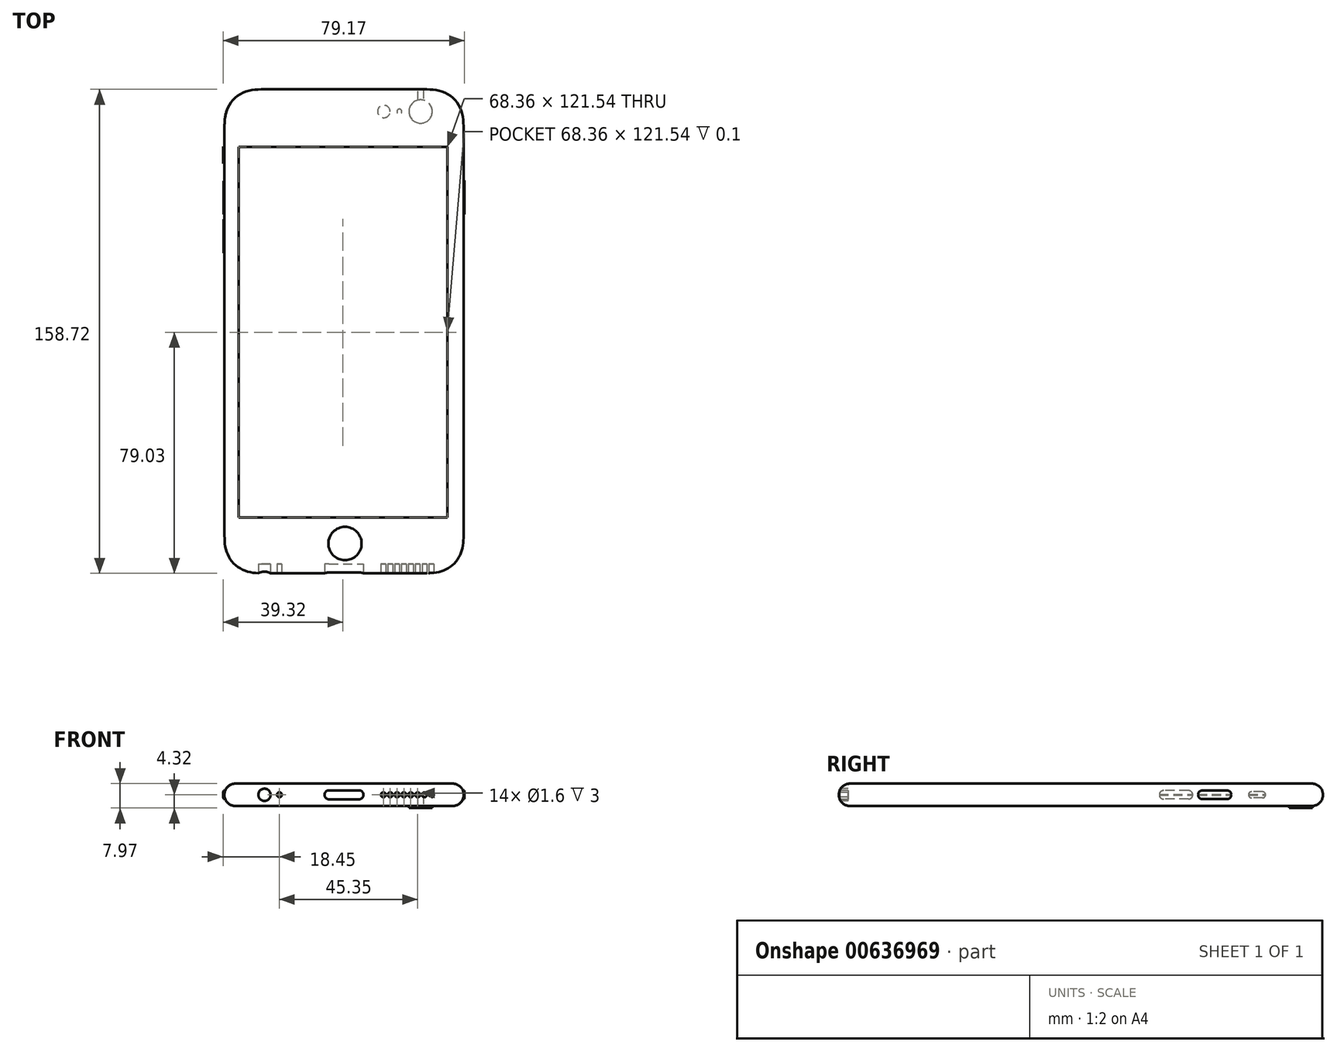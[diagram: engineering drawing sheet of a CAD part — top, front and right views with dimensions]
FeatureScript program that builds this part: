
annotation { "Feature Type Name" : "Feature", "Feature Type Description" : "" }
export const myFeature = defineFeature(function(context is Context, id is Id, definition is map)
    precondition{}
    {
        {
            var Q0;
            Q0=qCreatedBy(makeId("Top.planeOp"),FACE);
            var sketch = newSketch(context, id + "F0", { "sketchPlane" : qUnion([Q0])});
            skLineSegment(sketch, "E0.rect.bottom", {"start": v(25.09, -79.36) * mm, "end": v(-25.09, -79.36) * mm});
            skLineSegment(sketch, "E0.rect.top", {"start": v(25.09, 79.36) * mm, "end": v(-25.09, 79.36) * mm});
            skLineSegment(sketch, "E0.rect.left", {"start": v(39.22, -65.23) * mm, "end": v(39.22, 65.23) * mm});
            skLineSegment(sketch, "E0.rect.right", {"start": v(-39.22, -65.23) * mm, "end": v(-39.22, 65.23) * mm});
            skPoint(sketch, "E0.rect.middle", {"position": v(0, 0) * mm});
            skCircle(sketch, "E1", {"center": v(25.12, 72.09) * mm, "radius": 3.83 * mm});
            skCircle(sketch, "E2", {"center": v(18.16, 72.09) * mm, "radius": 0.8 * mm});
            skCircle(sketch, "E3", {"center": v(13.06, 72.09) * mm, "radius": 2.06 * mm});
            skLineSegment(sketch, "E4", {"start": v(-39.22, 72.1) * mm, "end": v(39.22, 72.1) * mm, "construction": true});
            skPoint(sketch, "E5.visualSharp", {"position": v(-39.22, 79.36) * mm});
            skFitSpline(sketch, "E6", {"points": [v(-25.09, 79.36) * mm, v(-29.02, 79.25) * mm, v(-32.83, 78.38) * mm, v(-36.09, 76.23) * mm, v(-38.24, 72.97) * mm, v(-39.1, 69.16) * mm, v(-39.22, 65.23) * mm], "startDerivative": vector(-8.98, 0) * mm, "endDerivative": vector(0, -8.98) * mm});
            skLineSegment(sketch, "E7", {"start": v(-25.09, 79.36) * mm, "end": v(-39.22, 79.36) * mm, "construction": true});
            skLineSegment(sketch, "E8", {"start": v(-39.22, 79.36) * mm, "end": v(-39.22, 65.23) * mm, "construction": true});
            skLineSegment(sketch, "E9", {"start": v(0, 79.36) * mm, "end": v(0, -79.36) * mm, "construction": true});
            skLineSegment(sketch, "E10", {"start": v(-39.22, 0) * mm, "end": v(39.22, 0) * mm, "construction": true});
            skFitSpline(sketch, "E11.MirrorCS", {"points": [v(25.09, 79.36) * mm, v(29.02, 79.25) * mm, v(32.83, 78.38) * mm, v(36.09, 76.23) * mm, v(38.24, 72.97) * mm, v(39.1, 69.16) * mm, v(39.22, 65.23) * mm], "startDerivative": vector(8.98, 0) * mm, "endDerivative": vector(0, -8.98) * mm});
            skFitSpline(sketch, "E12.MirrorCS", {"points": [v(-25.09, -79.36) * mm, v(-29.02, -79.25) * mm, v(-32.83, -78.38) * mm, v(-36.09, -76.23) * mm, v(-38.24, -72.97) * mm, v(-39.1, -69.16) * mm, v(-39.22, -65.23) * mm], "startDerivative": vector(-8.98, 0) * mm, "endDerivative": vector(0, 8.98) * mm});
            skFitSpline(sketch, "E13.MirrorCS", {"points": [v(25.09, -79.36) * mm, v(29.02, -79.25) * mm, v(32.83, -78.38) * mm, v(36.09, -76.23) * mm, v(38.24, -72.97) * mm, v(39.1, -69.16) * mm, v(39.22, -65.23) * mm], "startDerivative": vector(8.98, 0) * mm, "endDerivative": vector(0, 8.98) * mm});
            skCircle(sketch, "E14", {"center": v(0, 37.36) * mm, "radius": 11 * mm, "construction": true});
            skSolve(sketch);
        }
        {
            var Q0;
            Q0=makeQuery(id+"F0.imprint","IMPRINT",FACE,{"disambiguationData":[TD([[makeQuery(id+"F0.imprint","IMPRINT",EDGE,{"derivedFrom":sQuery(id+"F0.wireOp",EDGE,"E0.rect.bottom")}),-1.0]])]});
            var Q1;
            Q1=makeQuery(id+"F0.imprint","IMPRINT",FACE,{"disambiguationData":[TD([[makeQuery(id+"F0.imprint","IMPRINT",EDGE,{"derivedFrom":sQuery(id+"F0.wireOp",EDGE,"E1")}),1.0]])]});
            var Q2;
            Q2=makeQuery(id+"F0.imprint","IMPRINT",FACE,{"disambiguationData":[TD([[makeQuery(id+"F0.imprint","IMPRINT",EDGE,{"derivedFrom":sQuery(id+"F0.wireOp",EDGE,"E2")}),1.0]])]});
            var Q3;
            Q3=makeQuery(id+"F0.imprint","IMPRINT",FACE,{"disambiguationData":[TD([[makeQuery(id+"F0.imprint","IMPRINT",EDGE,{"derivedFrom":sQuery(id+"F0.wireOp",EDGE,"E3")}),1.0]])]});
            extrude(context, id + "F1", {"entities" : qUnion([Q0, Q1, Q2, Q3]), "depth" : 7.3 * mm});
        }
        {
            var Q0;
            Q0=makeQuery(id+"F0.imprint","IMPRINT",FACE,{"disambiguationData":[TD([[makeQuery(id+"F0.imprint","IMPRINT",EDGE,{"derivedFrom":sQuery(id+"F0.wireOp",EDGE,"E1")}),1.0]])]});
            extrude(context, id + "F2", {"entities" : qUnion([Q0]), "operationType" : NewBodyOperationType.ADD, "oppositeDirection" : true, "depth" : 0.67 * mm});
        }
        {
            var Q0;
            Q0=makeQuery(id+"F0.imprint","IMPRINT",FACE,{"disambiguationData":[TD([[makeQuery(id+"F0.imprint","IMPRINT",EDGE,{"derivedFrom":sQuery(id+"F0.wireOp",EDGE,"E3")}),1.0]])]});
            var Q1;
            Q1=makeQuery(id+"F0.imprint","IMPRINT",FACE,{"disambiguationData":[TD([[makeQuery(id+"F0.imprint","IMPRINT",EDGE,{"derivedFrom":sQuery(id+"F0.wireOp",EDGE,"E2")}),1.0]])]});
            extrude(context, id + "F3", {"entities" : qUnion([Q0, Q1]), "operationType" : NewBodyOperationType.REMOVE, "depth" : 0.1 * mm});
        }
        {
            var Q0;
            Q0=makeQuery(id+"F1.opExtrude","CAP_FACE",FACE,{"disambiguationData":[OSD([sQuery(id+"F0.wireOp",EDGE,"E0.rect.bottom"),sQuery(id+"F0.wireOp",EDGE,"E0.rect.top"),sQuery(id+"F0.wireOp",EDGE,"E0.rect.left"),sQuery(id+"F0.wireOp",EDGE,"E0.rect.right"),sQuery(id+"F0.wireOp",EDGE,"d7852d5b-fe0f-4a90-bdf2-04cff158e1f8.filletArc"),sQuery(id+"F0.wireOp",EDGE,"E5.filletArc"),sQuery(id+"F0.wireOp",EDGE,"7c06d2e9-cdf6-4879-9dee-aab3bc7c6033.filletArc"),sQuery(id+"F0.wireOp",EDGE,"93b3bdb9-dbb8-49f8-8f1e-002f612095da.filletArc")])],"isStart":false});
            var sketch = newSketch(context, id + "F4", { "sketchPlane" : qUnion([Q0])});
            skCircle(sketch, "E15", {"center": v(0.32, -69.6) * mm, "radius": 5.45 * mm});
            skLineSegment(sketch, "E16.bottom", {"start": v(-34.51, 60.44) * mm, "end": v(33.85, 60.44) * mm});
            skLineSegment(sketch, "E16.top", {"start": v(-34.5, -61.1) * mm, "end": v(33.85, -61.1) * mm});
            skLineSegment(sketch, "E16.left", {"start": v(-34.51, 60.44) * mm, "end": v(-34.5, -61.1) * mm});
            skLineSegment(sketch, "E16.right", {"start": v(33.85, 60.44) * mm, "end": v(33.85, -61.1) * mm});
            skSolve(sketch);
        }
        {
            var Q0;
            Q0=makeQuery(id+"F4.imprint","IMPRINT",FACE,{"disambiguationData":[TD([[makeQuery(id+"F4.imprint","IMPRINT",EDGE,{"derivedFrom":sQuery(id+"F4.wireOp",EDGE,"E15")}),1.0]])]});
            extrude(context, id + "F5", {"entities" : qUnion([Q0]), "operationType" : NewBodyOperationType.REMOVE, "oppositeDirection" : true, "depth" : 0.1 * mm});
        }
        {
            var Q0;
            Q0=makeQuery(id+"F4.imprint","IMPRINT",FACE,{"disambiguationData":[TD([[makeQuery(id+"F4.imprint","IMPRINT",EDGE,{"derivedFrom":sQuery(id+"F4.wireOp",EDGE,"E16.bottom")}),-1.0]])]});
            extrude(context, id + "F6", {"entities" : qUnion([Q0]), "operationType" : NewBodyOperationType.REMOVE, "oppositeDirection" : true, "depth" : 0.1 * mm});
        }
        {
            var Q0;
            Q0=makeQuery(id+"F1.opExtrude","SWEPT_FACE",FACE,{"disambiguationData":[OSD([sQuery(id+"F0.wireOp",EDGE,"E0.rect.bottom")])]});
            var sketch = newSketch(context, id + "F7", { "sketchPlane" : qUnion([Q0])});
            skLineSegment(sketch, "E17.0", {"start": v(25.09, 7.3) * mm, "end": v(-25.09, 7.3) * mm, "construction": true});
            skLineSegment(sketch, "E17.1", {"start": v(25.09, 0) * mm, "end": v(-25.09, 0) * mm, "construction": true});
            skLineSegment(sketch, "E17.2", {"start": v(39.22, 7.3) * mm, "end": v(39.22, 0) * mm, "construction": true});
            skLineSegment(sketch, "E17.3", {"start": v(-39.22, 7.3) * mm, "end": v(-39.22, 0) * mm, "construction": true});
            skFitSpline(sketch, "E17.4", {"points": [v(-24.74, 7.3) * mm, v(-29.45, 7.3) * mm, v(-34.16, 7.3) * mm, v(-38.87, 7.3) * mm], "construction": true});
            skFitSpline(sketch, "E17.5", {"points": [v(-24.74, 0) * mm, v(-29.45, 0) * mm, v(-34.16, 0) * mm, v(-38.87, 0) * mm], "construction": true});
            skFitSpline(sketch, "E17.6", {"points": [v(24.74, 0) * mm, v(29.45, 0) * mm, v(34.16, 0) * mm, v(38.87, 0) * mm], "construction": true});
            skFitSpline(sketch, "E17.7", {"points": [v(24.74, 7.3) * mm, v(29.45, 7.3) * mm, v(34.16, 7.3) * mm, v(38.87, 7.3) * mm], "construction": true});
            skLineSegment(sketch, "E18", {"start": v(0, 7.3) * mm, "end": v(0, 0) * mm, "construction": true});
            skLineSegment(sketch, "E19", {"start": v(-39.22, 3.65) * mm, "end": v(-6.4, 3.65) * mm, "construction": true});
            skLineSegment(sketch, "E20", {"start": v(-4.92, 5.12) * mm, "end": v(4.92, 5.12) * mm});
            skLineSegment(sketch, "E21", {"start": v(-4.92, 2.17) * mm, "end": v(4.92, 2.17) * mm});
            skLineSegment(sketch, "E22", {"start": v(-6.4, 3.65) * mm, "end": v(39.22, 3.65) * mm, "construction": true});
            skArc(sketch, "E23", {"start": v(-4.92, 5.13) * mm, "mid": v(-6.4, 3.65) * mm, "end": v(-4.92, 2.17) * mm});
            skArc(sketch, "E24", {"start": v(-4.92, 2.17) * mm, "mid": v(-3.44, 3.65) * mm, "end": v(-4.92, 5.13) * mm, "construction": true});
            skArc(sketch, "E25", {"start": v(4.92, 5.13) * mm, "mid": v(5.96, 4.7) * mm, "end": v(6.4, 3.65) * mm});
            skArc(sketch, "E26", {"start": v(4.92, 2.17) * mm, "mid": v(3.44, 3.65) * mm, "end": v(4.92, 5.13) * mm, "construction": true});
            skArc(sketch, "E27", {"start": v(6.4, 3.65) * mm, "mid": v(5.96, 2.6) * mm, "end": v(4.92, 2.17) * mm});
            skCircle(sketch, "E28", {"center": v(-26.09, 3.65) * mm, "radius": 2 * mm});
            skCircle(sketch, "E29", {"center": v(-21.2, 3.65) * mm, "radius": 0.8 * mm});
            skCircle(sketch, "E30", {"center": v(12.9, 3.65) * mm, "radius": 0.8 * mm});
            skCircle(sketch, "E31.1.0.0", {"center": v(15.15, 3.65) * mm, "radius": 0.8 * mm});
            skCircle(sketch, "E31.2.0.0", {"center": v(17.4, 3.65) * mm, "radius": 0.8 * mm});
            skCircle(sketch, "E31.3.0.0", {"center": v(19.65, 3.65) * mm, "radius": 0.8 * mm});
            skCircle(sketch, "E31.4.0.0", {"center": v(21.9, 3.65) * mm, "radius": 0.8 * mm});
            skCircle(sketch, "E31.5.0.0", {"center": v(24.15, 3.65) * mm, "radius": 0.8 * mm});
            skCircle(sketch, "E31.6.0.0", {"center": v(26.4, 3.65) * mm, "radius": 0.8 * mm});
            skCircle(sketch, "E31.7.0.0", {"center": v(28.65, 3.65) * mm, "radius": 0.8 * mm});
            skLineSegment(sketch, "E31.direction1", {"start": v(12.9, 3.65) * mm, "end": v(15.15, 3.65) * mm, "construction": true});
            skPoint(sketch, "E32", {"position": v(12.1, 3.65) * mm});
            skPoint(sketch, "E33", {"position": v(29.45, 3.65) * mm});
            skLineSegment(sketch, "E34.0", {"start": v(-25.09, 7.3) * mm, "end": v(-25.09, 0) * mm, "construction": true});
            skLineSegment(sketch, "E34.1", {"start": v(25.09, 7.3) * mm, "end": v(25.09, 0) * mm, "construction": true});
            skSolve(sketch);
        }
        {
            var Q0;
            Q0=makeQuery(id+"F1.opExtrude","SWEPT_FACE",FACE,{"disambiguationData":[OSD([sQuery(id+"F0.wireOp",EDGE,"E0.rect.left")])]});
            var sketch = newSketch(context, id + "F8", { "sketchPlane" : qUnion([Q0])});
            skLineSegment(sketch, "E35", {"start": v(-65.23, 2.25) * mm, "end": v(65.23, 2.25) * mm, "construction": true});
            skLineSegment(sketch, "E36", {"start": v(8.97, 4.69) * mm, "end": v(22.34, 4.7) * mm});
            skLineSegment(sketch, "E37", {"start": v(8.97, 2.25) * mm, "end": v(22.34, 2.25) * mm});
            skPoint(sketch, "E38", {"position": v(7.75, 3.47) * mm});
            skPoint(sketch, "E39", {"position": v(23.56, 3.47) * mm});
            skLineSegment(sketch, "E40", {"start": v(39.81, 2.25) * mm, "end": v(47.95, 2.25) * mm});
            skLineSegment(sketch, "E41", {"start": v(39.81, 5.05) * mm, "end": v(39.81, 5.05) * mm});
            skLineSegment(sketch, "E42", {"start": v(39.81, 3.65) * mm, "end": v(47.95, 3.65) * mm, "construction": true});
            skLineSegment(sketch, "E43", {"start": v(39.81, 5.05) * mm, "end": v(47.95, 5.05) * mm});
            skArc(sketch, "E44", {"start": v(47.95, 5.05) * mm, "mid": v(46.55, 3.65) * mm, "end": v(47.95, 2.25) * mm, "construction": true});
            skArc(sketch, "E45", {"start": v(47.95, 2.25) * mm, "mid": v(49.35, 3.65) * mm, "end": v(47.95, 5.05) * mm});
            skArc(sketch, "E46", {"start": v(39.81, 2.25) * mm, "mid": v(41.21, 3.65) * mm, "end": v(39.81, 5.05) * mm, "construction": true});
            skArc(sketch, "E47", {"start": v(39.81, 5.05) * mm, "mid": v(38.41, 3.65) * mm, "end": v(39.81, 2.25) * mm});
            skPoint(sketch, "E48", {"position": v(43.88, 3.65) * mm});
            skPoint(sketch, "E49", {"position": v(38.4, 3.65) * mm});
            skArc(sketch, "E50", {"start": v(8.97, 4.7) * mm, "mid": v(7.75, 3.47) * mm, "end": v(8.97, 2.25) * mm});
            skArc(sketch, "E51", {"start": v(8.97, 2.25) * mm, "mid": v(10.2, 3.47) * mm, "end": v(8.97, 4.7) * mm, "construction": true});
            skArc(sketch, "E52", {"start": v(22.34, 4.7) * mm, "mid": v(21.12, 3.47) * mm, "end": v(22.34, 2.25) * mm, "construction": true});
            skArc(sketch, "E53", {"start": v(22.34, 2.25) * mm, "mid": v(23.56, 3.47) * mm, "end": v(22.34, 4.7) * mm});
            skSolve(sketch);
        }
        {
            var Q0;
            Q0=makeQuery(id+"F1.opExtrude","SWEPT_FACE",FACE,{"disambiguationData":[OSD([sQuery(id+"F0.wireOp",EDGE,"E0.rect.right")])]});
            var sketch = newSketch(context, id + "F9", { "sketchPlane" : qUnion([Q0])});
            skLineSegment(sketch, "E54", {"start": v(-65.23, 3.63) * mm, "end": v(65.23, 3.63) * mm, "construction": true});
            skLineSegment(sketch, "E55", {"start": v(-60.58, 3.65) * mm, "end": v(-54.97, 3.65) * mm, "construction": true});
            skLineSegment(sketch, "E56", {"start": v(-59.6, 2.66) * mm, "end": v(-55.95, 2.66) * mm});
            skLineSegment(sketch, "E57", {"start": v(-59.6, 4.63) * mm, "end": v(-55.95, 4.63) * mm});
            skArc(sketch, "E58", {"start": v(-59.6, 2.66) * mm, "mid": v(-58.61, 3.64) * mm, "end": v(-59.6, 4.63) * mm, "construction": true});
            skArc(sketch, "E59", {"start": v(-59.6, 4.63) * mm, "mid": v(-60.58, 3.64) * mm, "end": v(-59.6, 2.66) * mm});
            skArc(sketch, "E60", {"start": v(-55.95, 2.66) * mm, "mid": v(-54.97, 3.65) * mm, "end": v(-55.95, 4.63) * mm});
            skArc(sketch, "E61", {"start": v(-55.95, 4.63) * mm, "mid": v(-56.94, 3.65) * mm, "end": v(-55.95, 2.66) * mm, "construction": true});
            skPoint(sketch, "E62.first.point", {"position": v(-49.28, 3.63) * mm});
            skPoint(sketch, "E62.second.point", {"position": v(-47.88, 2.23) * mm});
            skPoint(sketch, "E62.third.point", {"position": v(-47.88, 5.03) * mm});
            skPoint(sketch, "E63.first.point", {"position": v(-41.14, 3.63) * mm});
            skPoint(sketch, "E63.second.point", {"position": v(-39.74, 2.23) * mm});
            skPoint(sketch, "E63.third.point", {"position": v(-39.74, 5.03) * mm});
            skLineSegment(sketch, "E64", {"start": v(-47.88, 2.23) * mm, "end": v(-39.74, 2.23) * mm});
            skLineSegment(sketch, "E65", {"start": v(-47.88, 5.03) * mm, "end": v(-39.74, 5.03) * mm});
            skArc(sketch, "E66", {"start": v(-47.88, 5.03) * mm, "mid": v(-49.28, 3.63) * mm, "end": v(-47.88, 2.23) * mm});
            skArc(sketch, "E67", {"start": v(-47.88, 2.23) * mm, "mid": v(-46.48, 3.63) * mm, "end": v(-47.88, 5.03) * mm, "construction": true});
            skArc(sketch, "E68", {"start": v(-39.74, 2.23) * mm, "mid": v(-38.34, 3.63) * mm, "end": v(-39.74, 5.03) * mm});
            skArc(sketch, "E69", {"start": v(-39.74, 5.03) * mm, "mid": v(-41.14, 3.63) * mm, "end": v(-39.74, 2.23) * mm, "construction": true});
            skLineSegment(sketch, "E70", {"start": v(-47.88, 3.63) * mm, "end": v(-39.74, 3.63) * mm, "construction": true});
            skPoint(sketch, "E71", {"position": v(-43.81, 3.63) * mm});
            skLineSegment(sketch, "E72", {"start": v(-35.27, 2.23) * mm, "end": v(-27.13, 2.23) * mm});
            skLineSegment(sketch, "E73", {"start": v(-35.27, 5.03) * mm, "end": v(-27.13, 5.03) * mm});
            skPoint(sketch, "E74.third.point", {"position": v(-36.67, 3.63) * mm});
            skPoint(sketch, "E75.third.point", {"position": v(-25.73, 3.63) * mm});
            skLineSegment(sketch, "E76", {"start": v(-27.13, 3.63) * mm, "end": v(-35.27, 3.63) * mm, "construction": true});
            skPoint(sketch, "E77", {"position": v(-31.2, 3.63) * mm});
            skArc(sketch, "E78", {"start": v(-35.27, 2.23) * mm, "mid": v(-33.87, 3.63) * mm, "end": v(-35.27, 5.03) * mm, "construction": true});
            skArc(sketch, "E79", {"start": v(-35.27, 5.03) * mm, "mid": v(-36.67, 3.63) * mm, "end": v(-35.27, 2.23) * mm});
            skArc(sketch, "E80", {"start": v(-27.13, 5.03) * mm, "mid": v(-28.53, 3.63) * mm, "end": v(-27.13, 2.23) * mm, "construction": true});
            skArc(sketch, "E81", {"start": v(-27.13, 2.23) * mm, "mid": v(-25.73, 3.63) * mm, "end": v(-27.13, 5.03) * mm});
            skSolve(sketch);
        }
        {
            var Q0;
            Q0=makeQuery(id+"F1.opExtrude","CAP_EDGE",EDGE,{"disambiguationData":[OSD([sQuery(id+"F0.wireOp",EDGE,"E0.rect.top")])],"isStart":false});
            var Q1;
            Q1=makeQuery(id+"F1.opExtrude","CAP_EDGE",EDGE,{"disambiguationData":[OSD([sQuery(id+"F0.wireOp",EDGE,"E0.rect.top")])],"isStart":true});
            fillet(context, id + "F10", {"entities" : qUnion([Q0, Q1]), "radius" : (7.1 / 2) * mm, "tangentPropagation" : true, "allowEdgeOverflow" : false});
        }
        {
            var Q0;
            {var subQ0=makeQuery(id+"F1.opExtrude","SWEPT_EDGE",EDGE,{"disambiguationData":[OSD([sQuery(id+"F0.wireOp",EDGE,"E0.rect.bottom"),sQuery(id+"F0.wireOp",EDGE,"E12.MirrorCS")])]});var subQ1=sQuery(id+"F7.wireOp",EDGE,"E28");var subQ3=makeQuery(id+"F7.imprint","INTERSECT",VERTEX,{"disambiguationData":[OD(0.0)],"derivedFrom":[subQ0,subQ1]});Q0=makeQuery(id+"F7.imprint","IMPRINT",FACE,{"disambiguationData":[TD([[makeQuery(id+"F7.imprint","IMPRINT",EDGE,{"disambiguationData":[TD([[subQ3,-1.0]])],"derivedFrom":subQ1}),1.0]])]});}
            var Q1;
            Q1=makeQuery(id+"F7.imprint","IMPRINT",FACE,{"disambiguationData":[TD([[makeQuery(id+"F7.imprint","IMPRINT",EDGE,{"derivedFrom":sQuery(id+"F7.wireOp",EDGE,"E29")}),1.0]])]});
            var Q2;
            Q2=makeQuery(id+"F7.imprint","IMPRINT",FACE,{"disambiguationData":[TD([[makeQuery(id+"F7.imprint","IMPRINT",EDGE,{"derivedFrom":sQuery(id+"F7.wireOp",EDGE,"E20")}),-1.0]])]});
            var Q3;
            Q3=makeQuery(id+"F7.imprint","IMPRINT",FACE,{"disambiguationData":[TD([[makeQuery(id+"F7.imprint","IMPRINT",EDGE,{"derivedFrom":sQuery(id+"F7.wireOp",EDGE,"E30")}),1.0]])]});
            var Q4;
            Q4=makeQuery(id+"F7.imprint","IMPRINT",FACE,{"disambiguationData":[TD([[makeQuery(id+"F7.imprint","IMPRINT",EDGE,{"derivedFrom":sQuery(id+"F7.wireOp",EDGE,"E31.1.0.0")}),1.0]])]});
            var Q5;
            Q5=makeQuery(id+"F7.imprint","IMPRINT",FACE,{"disambiguationData":[TD([[makeQuery(id+"F7.imprint","IMPRINT",EDGE,{"derivedFrom":sQuery(id+"F7.wireOp",EDGE,"E31.2.0.0")}),1.0]])]});
            var Q6;
            Q6=makeQuery(id+"F7.imprint","IMPRINT",FACE,{"disambiguationData":[TD([[makeQuery(id+"F7.imprint","IMPRINT",EDGE,{"derivedFrom":sQuery(id+"F7.wireOp",EDGE,"E31.3.0.0")}),1.0]])]});
            var Q7;
            Q7=makeQuery(id+"F7.imprint","IMPRINT",FACE,{"disambiguationData":[TD([[makeQuery(id+"F7.imprint","IMPRINT",EDGE,{"derivedFrom":sQuery(id+"F7.wireOp",EDGE,"E31.4.0.0")}),1.0]])]});
            var Q8;
            Q8=makeQuery(id+"F7.imprint","IMPRINT",FACE,{"disambiguationData":[TD([[makeQuery(id+"F7.imprint","IMPRINT",EDGE,{"derivedFrom":sQuery(id+"F7.wireOp",EDGE,"E31.5.0.0")}),1.0]])]});
            var Q9;
            Q9=makeQuery(id+"F7.imprint","IMPRINT",FACE,{"disambiguationData":[TD([[makeQuery(id+"F7.imprint","IMPRINT",EDGE,{"derivedFrom":sQuery(id+"F7.wireOp",EDGE,"E31.6.0.0")}),1.0]])]});
            var Q10;
            Q10=makeQuery(id+"F7.imprint","IMPRINT",FACE,{"disambiguationData":[TD([[makeQuery(id+"F7.imprint","IMPRINT",EDGE,{"derivedFrom":sQuery(id+"F7.wireOp",EDGE,"E31.7.0.0")}),1.0]])]});
            var Q11;
            {var subQ0=makeQuery(id+"F1.opExtrude","SWEPT_EDGE",EDGE,{"disambiguationData":[OSD([sQuery(id+"F0.wireOp",EDGE,"E0.rect.bottom"),sQuery(id+"F0.wireOp",EDGE,"E12.MirrorCS")])]});var subQ1=sQuery(id+"F7.wireOp",EDGE,"E28");var subQ3=makeQuery(id+"F7.imprint","INTERSECT",VERTEX,{"disambiguationData":[OD(0.0)],"derivedFrom":[subQ0,subQ1]});Q11=makeQuery(id+"F7.imprint","IMPRINT",FACE,{"disambiguationData":[TD([[makeQuery(id+"F7.imprint","IMPRINT",EDGE,{"disambiguationData":[TD([[subQ3,1.0]])],"derivedFrom":subQ1}),1.0]])]});}
            extrude(context, id + "F11", {"entities" : qUnion([Q0, Q1, Q2, Q3, Q4, Q5, Q6, Q7, Q8, Q9, Q10, Q11]), "oppositeDirection" : true, "depth" : 3 * mm, "hasSecondDirection" : true, "secondDirectionOppositeDirection" : false, "secondDirectionDepth" : 1 * mm});
        }
        {
            var Q0;
            Q0=makeQuery(id+"F11.opExtrude","SWEPT_BODY",BODY,{"disambiguationData":[OSD([sQuery(id+"F7.wireOp",EDGE,"E28")])]});
            var Q1;
            Q1=makeQuery(id+"F11.opExtrude","SWEPT_BODY",BODY,{"disambiguationData":[OSD([sQuery(id+"F7.wireOp",EDGE,"E29")])]});
            var Q2;
            Q2=makeQuery(id+"F11.opExtrude","SWEPT_BODY",BODY,{"disambiguationData":[OSD([sQuery(id+"F7.wireOp",EDGE,"E30")])]});
            var Q3;
            Q3=makeQuery(id+"F11.opExtrude","SWEPT_BODY",BODY,{"disambiguationData":[OSD([sQuery(id+"F7.wireOp",EDGE,"E31.1.0.0")])]});
            var Q4;
            Q4=makeQuery(id+"F11.opExtrude","SWEPT_BODY",BODY,{"disambiguationData":[OSD([sQuery(id+"F7.wireOp",EDGE,"E31.2.0.0")])]});
            var Q5;
            Q5=makeQuery(id+"F11.opExtrude","SWEPT_BODY",BODY,{"disambiguationData":[OSD([sQuery(id+"F7.wireOp",EDGE,"E31.3.0.0")])]});
            var Q6;
            Q6=makeQuery(id+"F11.opExtrude","SWEPT_BODY",BODY,{"disambiguationData":[OSD([sQuery(id+"F7.wireOp",EDGE,"E31.4.0.0")])]});
            var Q7;
            Q7=makeQuery(id+"F11.opExtrude","SWEPT_BODY",BODY,{"disambiguationData":[OSD([sQuery(id+"F7.wireOp",EDGE,"E31.5.0.0")])]});
            var Q8;
            Q8=makeQuery(id+"F11.opExtrude","SWEPT_BODY",BODY,{"disambiguationData":[OSD([sQuery(id+"F7.wireOp",EDGE,"E31.6.0.0")])]});
            var Q9;
            Q9=makeQuery(id+"F11.opExtrude","SWEPT_BODY",BODY,{"disambiguationData":[OSD([sQuery(id+"F7.wireOp",EDGE,"E31.7.0.0")])]});
            var Q10;
            Q10=makeQuery(id+"F11.opExtrude","SWEPT_BODY",BODY,{"disambiguationData":[OSD([sQuery(id+"F7.wireOp",EDGE,"E20"),sQuery(id+"F7.wireOp",EDGE,"E21"),sQuery(id+"F7.wireOp",EDGE,"E23"),sQuery(id+"F7.wireOp",EDGE,"E25"),sQuery(id+"F7.wireOp",EDGE,"E27")])]});
            var Q11;
            Q11=makeQuery(id+"F1.opExtrude","SWEPT_BODY",BODY,{"disambiguationData":[OSD([sQuery(id+"F0.wireOp",EDGE,"E0.rect.bottom"),sQuery(id+"F0.wireOp",EDGE,"E0.rect.top"),sQuery(id+"F0.wireOp",EDGE,"E0.rect.left"),sQuery(id+"F0.wireOp",EDGE,"E0.rect.right"),sQuery(id+"F0.wireOp",EDGE,"E6"),sQuery(id+"F0.wireOp",EDGE,"E11.MirrorCS"),sQuery(id+"F0.wireOp",EDGE,"E12.MirrorCS"),sQuery(id+"F0.wireOp",EDGE,"E13.MirrorCS")])]});
            booleanBodies(context, id + "F12", {"operationType" : BooleanOperationType.SUBTRACTION, "tools" : qUnion([Q0, Q1, Q2, Q3, Q4, Q5, Q6, Q7, Q8, Q9, Q10]), "targets" : qUnion([Q11])});
        }
        {
            var Q0;
            Q0=makeQuery(id+"F8.imprint","IMPRINT",FACE,{"disambiguationData":[TD([[makeQuery(id+"F8.imprint","IMPRINT",EDGE,{"derivedFrom":sQuery(id+"F8.wireOp",EDGE,"E40")}),1.0]])]});
            extrude(context, id + "F13", {"entities" : qUnion([Q0]), "operationType" : NewBodyOperationType.ADD, "depth" : 0.3 * mm});
        }
        {
            var Q0;
            Q0=makeQuery(id+"F9.imprint","IMPRINT",FACE,{"disambiguationData":[TD([[makeQuery(id+"F9.imprint","IMPRINT",EDGE,{"derivedFrom":sQuery(id+"F9.wireOp",EDGE,"E72")}),1.0]])]});
            var Q1;
            Q1=makeQuery(id+"F9.imprint","IMPRINT",FACE,{"disambiguationData":[TD([[makeQuery(id+"F9.imprint","IMPRINT",EDGE,{"derivedFrom":sQuery(id+"F9.wireOp",EDGE,"E64")}),1.0]])]});
            extrude(context, id + "F14", {"entities" : qUnion([Q0, Q1]), "operationType" : NewBodyOperationType.ADD, "depth" : 0.3 * mm});
        }
        {
            var Q0;
            Q0=makeQuery(id+"F9.imprint","IMPRINT",FACE,{"disambiguationData":[TD([[makeQuery(id+"F9.imprint","IMPRINT",EDGE,{"derivedFrom":sQuery(id+"F9.wireOp",EDGE,"E56")}),1.0]])]});
            extrude(context, id + "F15", {"entities" : qUnion([Q0]), "operationType" : NewBodyOperationType.ADD, "depth" : 0.43 * mm});
        }
        {
            var Q0;
            Q0=makeQuery(id+"F1.opExtrude","SWEPT_BODY",BODY,{"disambiguationData":[OSD([sQuery(id+"F0.wireOp",EDGE,"E0.rect.bottom"),sQuery(id+"F0.wireOp",EDGE,"E0.rect.top"),sQuery(id+"F0.wireOp",EDGE,"E0.rect.left"),sQuery(id+"F0.wireOp",EDGE,"E0.rect.right"),sQuery(id+"F0.wireOp",EDGE,"E6"),sQuery(id+"F0.wireOp",EDGE,"E11.MirrorCS"),sQuery(id+"F0.wireOp",EDGE,"E12.MirrorCS"),sQuery(id+"F0.wireOp",EDGE,"E13.MirrorCS")])]});
            transform(context, id + "F16", {"entities" : qUnion([Q0]), "transformType" : TransformType.TRANSLATION_3D, "dx" : 0 * mm, "dy" : 0 * mm, "dz" : 0 * mm, "makeCopy" : true});
        }
    });
